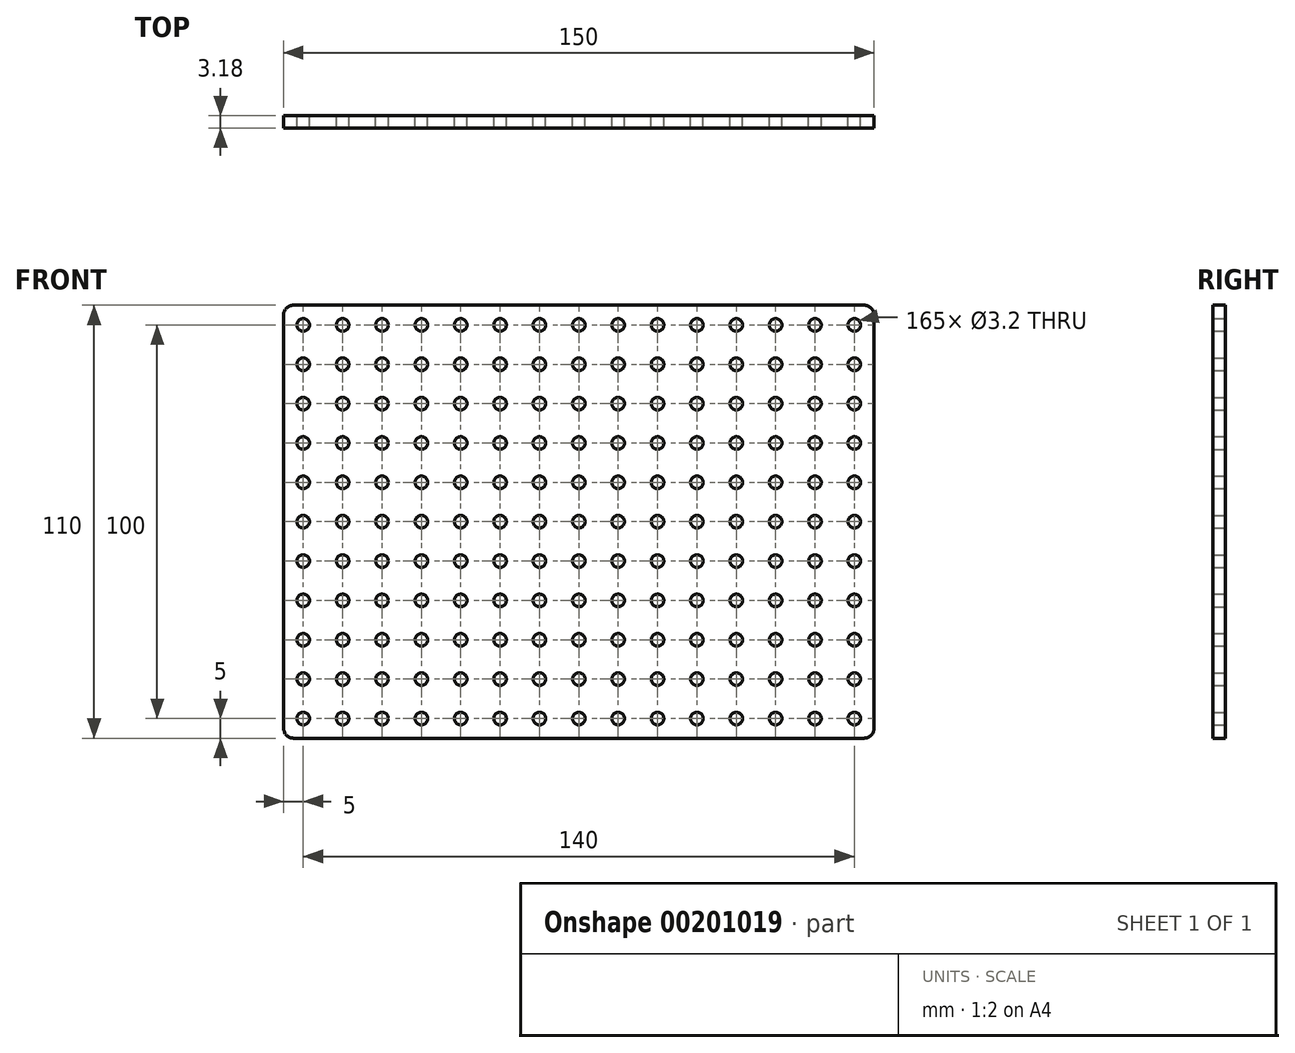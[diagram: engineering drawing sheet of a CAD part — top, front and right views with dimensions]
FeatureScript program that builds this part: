
annotation { "Feature Type Name" : "Feature", "Feature Type Description" : "" }
export const myFeature = defineFeature(function(context is Context, id is Id, definition is map)
    precondition{}
    {
        {
            var Q0;
            Q0=qCreatedBy(makeId("Front.planeOp"),FACE);
            var sketch = newSketch(context, id + "F0", { "sketchPlane" : qUnion([Q0])});
            skLineSegment(sketch, "E0.bottom", {"start": v(2.54, 0) * mm, "end": v(147.46, 0) * mm});
            skLineSegment(sketch, "E0.top", {"start": v(2.54, -110) * mm, "end": v(147.46, -110) * mm});
            skLineSegment(sketch, "E0.left", {"start": v(0, -2.54) * mm, "end": v(0, -107.46) * mm});
            skLineSegment(sketch, "E0.right", {"start": v(150, -2.54) * mm, "end": v(150, -107.46) * mm});
            skPoint(sketch, "E1.visualSharp", {"position": v(0, 0) * mm});
            skArc(sketch, "E1.filletArc", {"start": v(2.54, 0) * mm, "mid": v(0.74, -0.74) * mm, "end": v(0, -2.54) * mm});
            skPoint(sketch, "E2.visualSharp", {"position": v(0, -110) * mm});
            skArc(sketch, "E2.filletArc", {"start": v(0, -107.46) * mm, "mid": v(0.74, -109.26) * mm, "end": v(2.54, -110) * mm});
            skPoint(sketch, "E3.visualSharp", {"position": v(150, -110) * mm});
            skArc(sketch, "E3.filletArc", {"start": v(147.46, -110) * mm, "mid": v(149.26, -109.26) * mm, "end": v(150, -107.46) * mm});
            skPoint(sketch, "E4.visualSharp", {"position": v(150, 0) * mm});
            skArc(sketch, "E4.filletArc", {"start": v(150, -2.54) * mm, "mid": v(149.26, -0.74) * mm, "end": v(147.46, 0) * mm});
            skCircle(sketch, "E5", {"center": v(5, -5) * mm, "radius": 1.6 * mm});
            skCircle(sketch, "E6.0.1.0", {"center": v(5, -15) * mm, "radius": 1.6 * mm});
            skCircle(sketch, "E6.0.2.0", {"center": v(5, -25) * mm, "radius": 1.6 * mm});
            skCircle(sketch, "E6.0.3.0", {"center": v(5, -35) * mm, "radius": 1.6 * mm});
            skCircle(sketch, "E6.0.4.0", {"center": v(5, -45) * mm, "radius": 1.6 * mm});
            skCircle(sketch, "E6.0.5.0", {"center": v(5, -55) * mm, "radius": 1.6 * mm});
            skCircle(sketch, "E6.0.6.0", {"center": v(5, -65) * mm, "radius": 1.6 * mm});
            skCircle(sketch, "E6.0.7.0", {"center": v(5, -75) * mm, "radius": 1.6 * mm});
            skCircle(sketch, "E6.0.8.0", {"center": v(5, -85) * mm, "radius": 1.6 * mm});
            skCircle(sketch, "E6.0.9.0", {"center": v(5, -95) * mm, "radius": 1.6 * mm});
            skCircle(sketch, "E6.0.10.0", {"center": v(5, -105) * mm, "radius": 1.6 * mm});
            skCircle(sketch, "E6.1.0.0", {"center": v(15, -5) * mm, "radius": 1.6 * mm});
            skCircle(sketch, "E6.1.1.0", {"center": v(15, -15) * mm, "radius": 1.6 * mm});
            skCircle(sketch, "E6.1.2.0", {"center": v(15, -25) * mm, "radius": 1.6 * mm});
            skCircle(sketch, "E6.1.3.0", {"center": v(15, -35) * mm, "radius": 1.6 * mm});
            skCircle(sketch, "E6.1.4.0", {"center": v(15, -45) * mm, "radius": 1.6 * mm});
            skCircle(sketch, "E6.1.5.0", {"center": v(15, -55) * mm, "radius": 1.6 * mm});
            skCircle(sketch, "E6.1.6.0", {"center": v(15, -65) * mm, "radius": 1.6 * mm});
            skCircle(sketch, "E6.1.7.0", {"center": v(15, -75) * mm, "radius": 1.6 * mm});
            skCircle(sketch, "E6.1.8.0", {"center": v(15, -85) * mm, "radius": 1.6 * mm});
            skCircle(sketch, "E6.1.9.0", {"center": v(15, -95) * mm, "radius": 1.6 * mm});
            skCircle(sketch, "E6.1.10.0", {"center": v(15, -105) * mm, "radius": 1.6 * mm});
            skCircle(sketch, "E6.2.0.0", {"center": v(25, -5) * mm, "radius": 1.6 * mm});
            skCircle(sketch, "E6.2.1.0", {"center": v(25, -15) * mm, "radius": 1.6 * mm});
            skCircle(sketch, "E6.2.2.0", {"center": v(25, -25) * mm, "radius": 1.6 * mm});
            skCircle(sketch, "E6.2.3.0", {"center": v(25, -35) * mm, "radius": 1.6 * mm});
            skCircle(sketch, "E6.2.4.0", {"center": v(25, -45) * mm, "radius": 1.6 * mm});
            skCircle(sketch, "E6.2.5.0", {"center": v(25, -55) * mm, "radius": 1.6 * mm});
            skCircle(sketch, "E6.2.6.0", {"center": v(25, -65) * mm, "radius": 1.6 * mm});
            skCircle(sketch, "E6.2.7.0", {"center": v(25, -75) * mm, "radius": 1.6 * mm});
            skCircle(sketch, "E6.2.8.0", {"center": v(25, -85) * mm, "radius": 1.6 * mm});
            skCircle(sketch, "E6.2.9.0", {"center": v(25, -95) * mm, "radius": 1.6 * mm});
            skCircle(sketch, "E6.2.10.0", {"center": v(25, -105) * mm, "radius": 1.6 * mm});
            skCircle(sketch, "E6.3.0.0", {"center": v(35, -5) * mm, "radius": 1.6 * mm});
            skCircle(sketch, "E6.3.1.0", {"center": v(35, -15) * mm, "radius": 1.6 * mm});
            skCircle(sketch, "E6.3.2.0", {"center": v(35, -25) * mm, "radius": 1.6 * mm});
            skCircle(sketch, "E6.3.3.0", {"center": v(35, -35) * mm, "radius": 1.6 * mm});
            skCircle(sketch, "E6.3.4.0", {"center": v(35, -45) * mm, "radius": 1.6 * mm});
            skCircle(sketch, "E6.3.5.0", {"center": v(35, -55) * mm, "radius": 1.6 * mm});
            skCircle(sketch, "E6.3.6.0", {"center": v(35, -65) * mm, "radius": 1.6 * mm});
            skCircle(sketch, "E6.3.7.0", {"center": v(35, -75) * mm, "radius": 1.6 * mm});
            skCircle(sketch, "E6.3.8.0", {"center": v(35, -85) * mm, "radius": 1.6 * mm});
            skCircle(sketch, "E6.3.9.0", {"center": v(35, -95) * mm, "radius": 1.6 * mm});
            skCircle(sketch, "E6.3.10.0", {"center": v(35, -105) * mm, "radius": 1.6 * mm});
            skCircle(sketch, "E6.4.0.0", {"center": v(45, -5) * mm, "radius": 1.6 * mm});
            skCircle(sketch, "E6.4.1.0", {"center": v(45, -15) * mm, "radius": 1.6 * mm});
            skCircle(sketch, "E6.4.2.0", {"center": v(45, -25) * mm, "radius": 1.6 * mm});
            skCircle(sketch, "E6.4.3.0", {"center": v(45, -35) * mm, "radius": 1.6 * mm});
            skCircle(sketch, "E6.4.4.0", {"center": v(45, -45) * mm, "radius": 1.6 * mm});
            skCircle(sketch, "E6.4.5.0", {"center": v(45, -55) * mm, "radius": 1.6 * mm});
            skCircle(sketch, "E6.4.6.0", {"center": v(45, -65) * mm, "radius": 1.6 * mm});
            skCircle(sketch, "E6.4.7.0", {"center": v(45, -75) * mm, "radius": 1.6 * mm});
            skCircle(sketch, "E6.4.8.0", {"center": v(45, -85) * mm, "radius": 1.6 * mm});
            skCircle(sketch, "E6.4.9.0", {"center": v(45, -95) * mm, "radius": 1.6 * mm});
            skCircle(sketch, "E6.4.10.0", {"center": v(45, -105) * mm, "radius": 1.6 * mm});
            skCircle(sketch, "E6.5.0.0", {"center": v(55, -5) * mm, "radius": 1.6 * mm});
            skCircle(sketch, "E6.5.1.0", {"center": v(55, -15) * mm, "radius": 1.6 * mm});
            skCircle(sketch, "E6.5.2.0", {"center": v(55, -25) * mm, "radius": 1.6 * mm});
            skCircle(sketch, "E6.5.3.0", {"center": v(55, -35) * mm, "radius": 1.6 * mm});
            skCircle(sketch, "E6.5.4.0", {"center": v(55, -45) * mm, "radius": 1.6 * mm});
            skCircle(sketch, "E6.5.5.0", {"center": v(55, -55) * mm, "radius": 1.6 * mm});
            skCircle(sketch, "E6.5.6.0", {"center": v(55, -65) * mm, "radius": 1.6 * mm});
            skCircle(sketch, "E6.5.7.0", {"center": v(55, -75) * mm, "radius": 1.6 * mm});
            skCircle(sketch, "E6.5.8.0", {"center": v(55, -85) * mm, "radius": 1.6 * mm});
            skCircle(sketch, "E6.5.9.0", {"center": v(55, -95) * mm, "radius": 1.6 * mm});
            skCircle(sketch, "E6.5.10.0", {"center": v(55, -105) * mm, "radius": 1.6 * mm});
            skCircle(sketch, "E6.6.0.0", {"center": v(65, -5) * mm, "radius": 1.6 * mm});
            skCircle(sketch, "E6.6.1.0", {"center": v(65, -15) * mm, "radius": 1.6 * mm});
            skCircle(sketch, "E6.6.2.0", {"center": v(65, -25) * mm, "radius": 1.6 * mm});
            skCircle(sketch, "E6.6.3.0", {"center": v(65, -35) * mm, "radius": 1.6 * mm});
            skCircle(sketch, "E6.6.4.0", {"center": v(65, -45) * mm, "radius": 1.6 * mm});
            skCircle(sketch, "E6.6.5.0", {"center": v(65, -55) * mm, "radius": 1.6 * mm});
            skCircle(sketch, "E6.6.6.0", {"center": v(65, -65) * mm, "radius": 1.6 * mm});
            skCircle(sketch, "E6.6.7.0", {"center": v(65, -75) * mm, "radius": 1.6 * mm});
            skCircle(sketch, "E6.6.8.0", {"center": v(65, -85) * mm, "radius": 1.6 * mm});
            skCircle(sketch, "E6.6.9.0", {"center": v(65, -95) * mm, "radius": 1.6 * mm});
            skCircle(sketch, "E6.6.10.0", {"center": v(65, -105) * mm, "radius": 1.6 * mm});
            skCircle(sketch, "E6.7.0.0", {"center": v(75, -5) * mm, "radius": 1.6 * mm});
            skCircle(sketch, "E6.7.1.0", {"center": v(75, -15) * mm, "radius": 1.6 * mm});
            skCircle(sketch, "E6.7.2.0", {"center": v(75, -25) * mm, "radius": 1.6 * mm});
            skCircle(sketch, "E6.7.3.0", {"center": v(75, -35) * mm, "radius": 1.6 * mm});
            skCircle(sketch, "E6.7.4.0", {"center": v(75, -45) * mm, "radius": 1.6 * mm});
            skCircle(sketch, "E6.7.5.0", {"center": v(75, -55) * mm, "radius": 1.6 * mm});
            skCircle(sketch, "E6.7.6.0", {"center": v(75, -65) * mm, "radius": 1.6 * mm});
            skCircle(sketch, "E6.7.7.0", {"center": v(75, -75) * mm, "radius": 1.6 * mm});
            skCircle(sketch, "E6.7.8.0", {"center": v(75, -85) * mm, "radius": 1.6 * mm});
            skCircle(sketch, "E6.7.9.0", {"center": v(75, -95) * mm, "radius": 1.6 * mm});
            skCircle(sketch, "E6.7.10.0", {"center": v(75, -105) * mm, "radius": 1.6 * mm});
            skCircle(sketch, "E6.8.0.0", {"center": v(85, -5) * mm, "radius": 1.6 * mm});
            skCircle(sketch, "E6.8.1.0", {"center": v(85, -15) * mm, "radius": 1.6 * mm});
            skCircle(sketch, "E6.8.2.0", {"center": v(85, -25) * mm, "radius": 1.6 * mm});
            skCircle(sketch, "E6.8.3.0", {"center": v(85, -35) * mm, "radius": 1.6 * mm});
            skCircle(sketch, "E6.8.4.0", {"center": v(85, -45) * mm, "radius": 1.6 * mm});
            skCircle(sketch, "E6.8.5.0", {"center": v(85, -55) * mm, "radius": 1.6 * mm});
            skCircle(sketch, "E6.8.6.0", {"center": v(85, -65) * mm, "radius": 1.6 * mm});
            skCircle(sketch, "E6.8.7.0", {"center": v(85, -75) * mm, "radius": 1.6 * mm});
            skCircle(sketch, "E6.8.8.0", {"center": v(85, -85) * mm, "radius": 1.6 * mm});
            skCircle(sketch, "E6.8.9.0", {"center": v(85, -95) * mm, "radius": 1.6 * mm});
            skCircle(sketch, "E6.8.10.0", {"center": v(85, -105) * mm, "radius": 1.6 * mm});
            skCircle(sketch, "E6.9.0.0", {"center": v(95, -5) * mm, "radius": 1.6 * mm});
            skCircle(sketch, "E6.9.1.0", {"center": v(95, -15) * mm, "radius": 1.6 * mm});
            skCircle(sketch, "E6.9.2.0", {"center": v(95, -25) * mm, "radius": 1.6 * mm});
            skCircle(sketch, "E6.9.3.0", {"center": v(95, -35) * mm, "radius": 1.6 * mm});
            skCircle(sketch, "E6.9.4.0", {"center": v(95, -45) * mm, "radius": 1.6 * mm});
            skCircle(sketch, "E6.9.5.0", {"center": v(95, -55) * mm, "radius": 1.6 * mm});
            skCircle(sketch, "E6.9.6.0", {"center": v(95, -65) * mm, "radius": 1.6 * mm});
            skCircle(sketch, "E6.9.7.0", {"center": v(95, -75) * mm, "radius": 1.6 * mm});
            skCircle(sketch, "E6.9.8.0", {"center": v(95, -85) * mm, "radius": 1.6 * mm});
            skCircle(sketch, "E6.9.9.0", {"center": v(95, -95) * mm, "radius": 1.6 * mm});
            skCircle(sketch, "E6.9.10.0", {"center": v(95, -105) * mm, "radius": 1.6 * mm});
            skCircle(sketch, "E6.10.0.0", {"center": v(105, -5) * mm, "radius": 1.6 * mm});
            skCircle(sketch, "E6.10.1.0", {"center": v(105, -15) * mm, "radius": 1.6 * mm});
            skCircle(sketch, "E6.10.2.0", {"center": v(105, -25) * mm, "radius": 1.6 * mm});
            skCircle(sketch, "E6.10.3.0", {"center": v(105, -35) * mm, "radius": 1.6 * mm});
            skCircle(sketch, "E6.10.4.0", {"center": v(105, -45) * mm, "radius": 1.6 * mm});
            skCircle(sketch, "E6.10.5.0", {"center": v(105, -55) * mm, "radius": 1.6 * mm});
            skCircle(sketch, "E6.10.6.0", {"center": v(105, -65) * mm, "radius": 1.6 * mm});
            skCircle(sketch, "E6.10.7.0", {"center": v(105, -75) * mm, "radius": 1.6 * mm});
            skCircle(sketch, "E6.10.8.0", {"center": v(105, -85) * mm, "radius": 1.6 * mm});
            skCircle(sketch, "E6.10.9.0", {"center": v(105, -95) * mm, "radius": 1.6 * mm});
            skCircle(sketch, "E6.10.10.0", {"center": v(105, -105) * mm, "radius": 1.6 * mm});
            skCircle(sketch, "E6.11.0.0", {"center": v(115, -5) * mm, "radius": 1.6 * mm});
            skCircle(sketch, "E6.11.1.0", {"center": v(115, -15) * mm, "radius": 1.6 * mm});
            skCircle(sketch, "E6.11.2.0", {"center": v(115, -25) * mm, "radius": 1.6 * mm});
            skCircle(sketch, "E6.11.3.0", {"center": v(115, -35) * mm, "radius": 1.6 * mm});
            skCircle(sketch, "E6.11.4.0", {"center": v(115, -45) * mm, "radius": 1.6 * mm});
            skCircle(sketch, "E6.11.5.0", {"center": v(115, -55) * mm, "radius": 1.6 * mm});
            skCircle(sketch, "E6.11.6.0", {"center": v(115, -65) * mm, "radius": 1.6 * mm});
            skCircle(sketch, "E6.11.7.0", {"center": v(115, -75) * mm, "radius": 1.6 * mm});
            skCircle(sketch, "E6.11.8.0", {"center": v(115, -85) * mm, "radius": 1.6 * mm});
            skCircle(sketch, "E6.11.9.0", {"center": v(115, -95) * mm, "radius": 1.6 * mm});
            skCircle(sketch, "E6.11.10.0", {"center": v(115, -105) * mm, "radius": 1.6 * mm});
            skCircle(sketch, "E6.12.0.0", {"center": v(125, -5) * mm, "radius": 1.6 * mm});
            skCircle(sketch, "E6.12.1.0", {"center": v(125, -15) * mm, "radius": 1.6 * mm});
            skCircle(sketch, "E6.12.2.0", {"center": v(125, -25) * mm, "radius": 1.6 * mm});
            skCircle(sketch, "E6.12.3.0", {"center": v(125, -35) * mm, "radius": 1.6 * mm});
            skCircle(sketch, "E6.12.4.0", {"center": v(125, -45) * mm, "radius": 1.6 * mm});
            skCircle(sketch, "E6.12.5.0", {"center": v(125, -55) * mm, "radius": 1.6 * mm});
            skCircle(sketch, "E6.12.6.0", {"center": v(125, -65) * mm, "radius": 1.6 * mm});
            skCircle(sketch, "E6.12.7.0", {"center": v(125, -75) * mm, "radius": 1.6 * mm});
            skCircle(sketch, "E6.12.8.0", {"center": v(125, -85) * mm, "radius": 1.6 * mm});
            skCircle(sketch, "E6.12.9.0", {"center": v(125, -95) * mm, "radius": 1.6 * mm});
            skCircle(sketch, "E6.12.10.0", {"center": v(125, -105) * mm, "radius": 1.6 * mm});
            skCircle(sketch, "E6.13.0.0", {"center": v(135, -5) * mm, "radius": 1.6 * mm});
            skCircle(sketch, "E6.13.1.0", {"center": v(135, -15) * mm, "radius": 1.6 * mm});
            skCircle(sketch, "E6.13.2.0", {"center": v(135, -25) * mm, "radius": 1.6 * mm});
            skCircle(sketch, "E6.13.3.0", {"center": v(135, -35) * mm, "radius": 1.6 * mm});
            skCircle(sketch, "E6.13.4.0", {"center": v(135, -45) * mm, "radius": 1.6 * mm});
            skCircle(sketch, "E6.13.5.0", {"center": v(135, -55) * mm, "radius": 1.6 * mm});
            skCircle(sketch, "E6.13.6.0", {"center": v(135, -65) * mm, "radius": 1.6 * mm});
            skCircle(sketch, "E6.13.7.0", {"center": v(135, -75) * mm, "radius": 1.6 * mm});
            skCircle(sketch, "E6.13.8.0", {"center": v(135, -85) * mm, "radius": 1.6 * mm});
            skCircle(sketch, "E6.13.9.0", {"center": v(135, -95) * mm, "radius": 1.6 * mm});
            skCircle(sketch, "E6.13.10.0", {"center": v(135, -105) * mm, "radius": 1.6 * mm});
            skCircle(sketch, "E6.14.0.0", {"center": v(145, -5) * mm, "radius": 1.6 * mm});
            skCircle(sketch, "E6.14.1.0", {"center": v(145, -15) * mm, "radius": 1.6 * mm});
            skCircle(sketch, "E6.14.2.0", {"center": v(145, -25) * mm, "radius": 1.6 * mm});
            skCircle(sketch, "E6.14.3.0", {"center": v(145, -35) * mm, "radius": 1.6 * mm});
            skCircle(sketch, "E6.14.4.0", {"center": v(145, -45) * mm, "radius": 1.6 * mm});
            skCircle(sketch, "E6.14.5.0", {"center": v(145, -55) * mm, "radius": 1.6 * mm});
            skCircle(sketch, "E6.14.6.0", {"center": v(145, -65) * mm, "radius": 1.6 * mm});
            skCircle(sketch, "E6.14.7.0", {"center": v(145, -75) * mm, "radius": 1.6 * mm});
            skCircle(sketch, "E6.14.8.0", {"center": v(145, -85) * mm, "radius": 1.6 * mm});
            skCircle(sketch, "E6.14.9.0", {"center": v(145, -95) * mm, "radius": 1.6 * mm});
            skCircle(sketch, "E6.14.10.0", {"center": v(145, -105) * mm, "radius": 1.6 * mm});
            skLineSegment(sketch, "E6.direction1", {"start": v(5, -5) * mm, "end": v(15, -5) * mm, "construction": true});
            skLineSegment(sketch, "E6.direction2", {"start": v(5, -5) * mm, "end": v(5, -15) * mm, "construction": true});
            skSolve(sketch);
        }
        {
            var Q0;
            Q0=makeQuery(id+"F0.imprint","IMPRINT",FACE,{"disambiguationData":[TD([[makeQuery(id+"F0.imprint","IMPRINT",EDGE,{"derivedFrom":sQuery(id+"F0.wireOp",EDGE,"E0.bottom")}),-1.0]])]});
            extrude(context, id + "F1", {"entities" : qUnion([Q0]), "depth" : 3.17 * mm});
        }
    });
